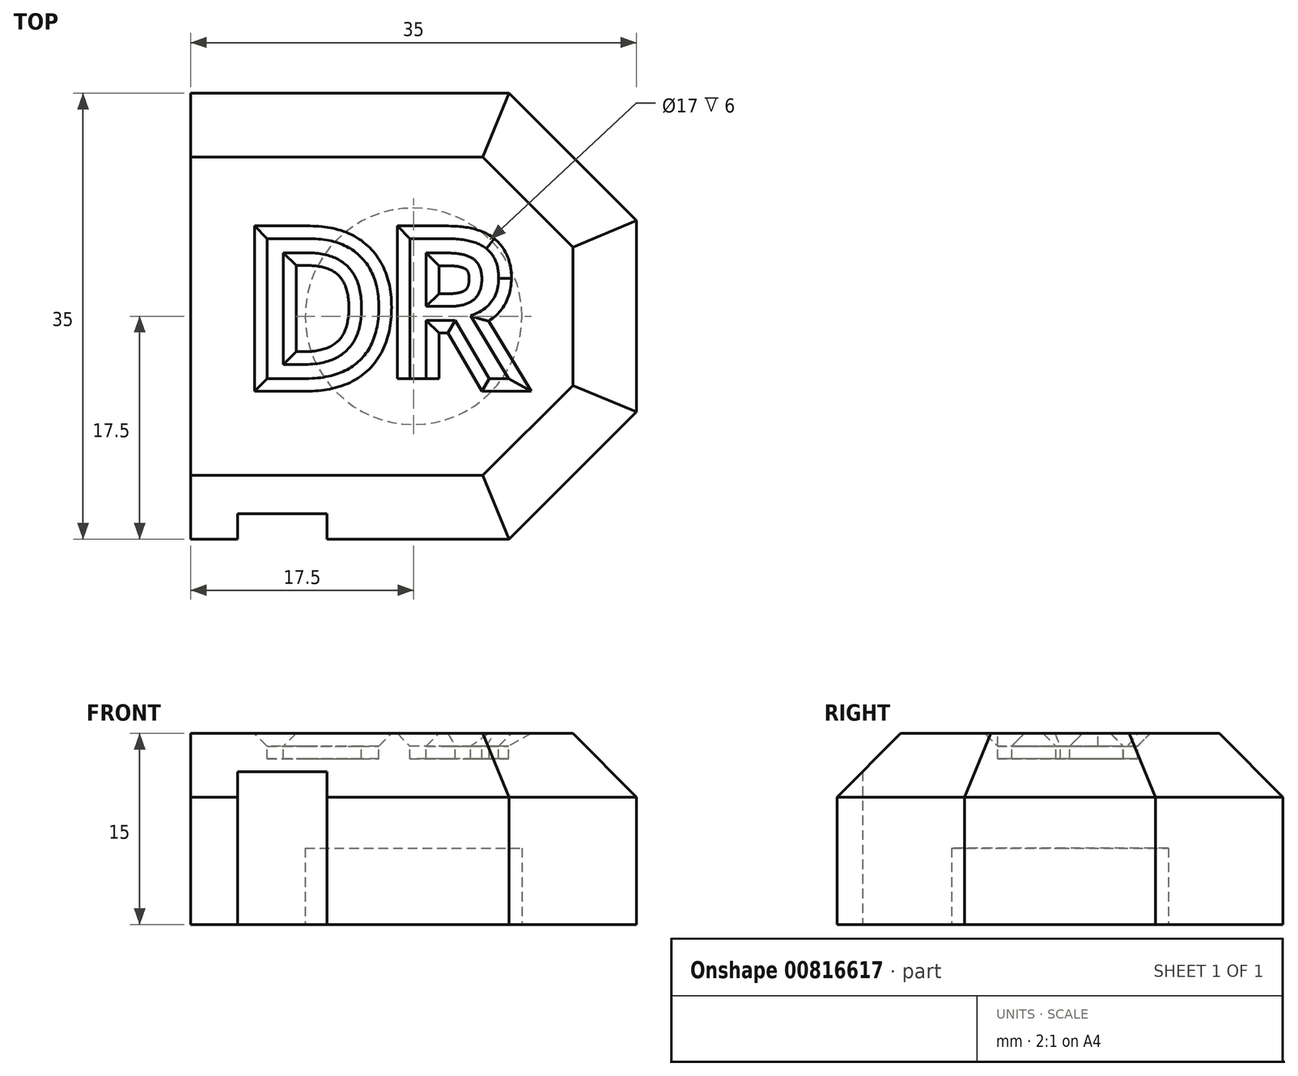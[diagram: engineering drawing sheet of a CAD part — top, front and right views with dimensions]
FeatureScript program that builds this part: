
annotation { "Feature Type Name" : "Feature", "Feature Type Description" : "" }
export const myFeature = defineFeature(function(context is Context, id is Id, definition is map)
    precondition{}
    {
        {
            var Q0;
            Q0=qCreatedBy(makeId("Top.planeOp"),FACE);
            var sketch = newSketch(context, id + "F0", { "sketchPlane" : qUnion([Q0])});
            skLineSegment(sketch, "E0.bottom", {"start": v(-17.5, 17.5) * mm, "end": v(17.5, 17.5) * mm});
            skLineSegment(sketch, "E0.top", {"start": v(-17.5, -17.5) * mm, "end": v(17.5, -17.5) * mm});
            skLineSegment(sketch, "E0.left", {"start": v(-17.5, 17.5) * mm, "end": v(-17.5, -17.5) * mm});
            skLineSegment(sketch, "E0.right", {"start": v(17.5, 17.5) * mm, "end": v(17.5, -17.5) * mm});
            skPoint(sketch, "E0.middle", {"position": v(0, 0) * mm});
            skSolve(sketch);
        }
        {
            var Q0;
            Q0=makeQuery(id+"F0.imprint","IMPRINT",FACE,{"disambiguationData":[TD([[makeQuery(id+"F0.imprint","IMPRINT",EDGE,{"derivedFrom":sQuery(id+"F0.wireOp",EDGE,"E0.bottom")}),-1.0]])]});
            extrude(context, id + "F1", {"entities" : qUnion([Q0]), "depth" : 15 * mm, "offsetDistance" : 25 * mm});
        }
        {
            var Q0;
            Q0=makeQuery(id+"F1.opExtrude","SWEPT_EDGE",EDGE,{"disambiguationData":[OSD([sQuery(id+"F0.wireOp",EDGE,"E0.top"),sQuery(id+"F0.wireOp",EDGE,"E0.right")])]});
            var Q1;
            Q1=makeQuery(id+"F1.opExtrude","SWEPT_EDGE",EDGE,{"disambiguationData":[OSD([sQuery(id+"F0.wireOp",EDGE,"E0.bottom"),sQuery(id+"F0.wireOp",EDGE,"E0.right")])]});
            chamfer(context, id + "F2", {"entities" : qUnion([Q0, Q1]), "width" : 10 * mm, "tangentPropagation" : true});
        }
        {
            var Q0;
            Q0=makeQuery(id+"F1.opExtrude","SWEPT_FACE",FACE,{"disambiguationData":[OSD([sQuery(id+"F0.wireOp",EDGE,"E0.top")])]});
            var sketch = newSketch(context, id + "F3", { "sketchPlane" : qUnion([Q0])});
            skLineSegment(sketch, "E1.bottom", {"start": v(-13.8, 12) * mm, "end": v(-6.8, 12) * mm});
            skLineSegment(sketch, "E1.top", {"start": v(-13.8, 0) * mm, "end": v(-6.8, 0) * mm});
            skLineSegment(sketch, "E1.left", {"start": v(-13.8, 12) * mm, "end": v(-13.8, 0) * mm});
            skLineSegment(sketch, "E1.right", {"start": v(-6.8, 12) * mm, "end": v(-6.8, 0) * mm});
            skSolve(sketch);
        }
        {
            var Q0;
            Q0=makeQuery(id+"F3.imprint","IMPRINT",FACE,{"disambiguationData":[TD([[makeQuery(id+"F3.imprint","IMPRINT",EDGE,{"derivedFrom":sQuery(id+"F3.wireOp",EDGE,"E1.bottom")}),-1.0]])]});
            extrude(context, id + "F4", {"entities" : qUnion([Q0]), "operationType" : NewBodyOperationType.REMOVE, "oppositeDirection" : true, "depth" : 2 * mm, "offsetDistance" : 25 * mm});
        }
        {
            var Q0;
            Q0=makeQuery(id+"F1.opExtrude","CAP_FACE",FACE,{"disambiguationData":[OSD([sQuery(id+"F0.wireOp",EDGE,"E0.bottom"),sQuery(id+"F0.wireOp",EDGE,"E0.top"),sQuery(id+"F0.wireOp",EDGE,"E0.left"),sQuery(id+"F0.wireOp",EDGE,"E0.right")])],"isStart":true});
            var sketch = newSketch(context, id + "F5", { "sketchPlane" : qUnion([Q0])});
            skCircle(sketch, "E2", {"center": v(0, 0) * mm, "radius": 8.5 * mm});
            skSolve(sketch);
        }
        {
            var Q0;
            Q0 = qSketchRegion(id + "F5", true);
            extrude(context, id + "F6", {"entities" : qUnion([Q0]), "operationType" : NewBodyOperationType.REMOVE, "oppositeDirection" : true, "depth" : 6 * mm, "offsetDistance" : 25 * mm});
        }
        {
            var Q0;
            {var subQ0=sQuery(id+"F0.wireOp",EDGE,"E0.right");var subQ1=sQuery(id+"F0.wireOp",EDGE,"E0.top");Q0=makeQuery(id+"F2.opChamfer","BLEND_EDGE",EDGE,{"blendedFrom":[makeQuery(id+"F1.opExtrude","SWEPT_EDGE",EDGE,{"disambiguationData":[OSD([subQ1,subQ0])]}),makeQuery(id+"F1.opExtrude","CAP_FACE",FACE,{"disambiguationData":[OSD([sQuery(id+"F0.wireOp",EDGE,"E0.bottom"),subQ1,sQuery(id+"F0.wireOp",EDGE,"E0.left"),subQ0])],"isStart":false})],"blendedInto":[makeQuery(id+"F1.opExtrude","CAP_FACE",FACE,{"disambiguationData":[OSD([sQuery(id+"F0.wireOp",EDGE,"E0.bottom"),subQ1,sQuery(id+"F0.wireOp",EDGE,"E0.left"),subQ0])],"isStart":false})]});}
            var Q1;
            Q1=makeQuery(id+"F1.opExtrude","CAP_EDGE",EDGE,{"disambiguationData":[OSD([sQuery(id+"F0.wireOp",EDGE,"E0.right")])],"isStart":false});
            var Q2;
            Q2=makeQuery(id+"F1.opExtrude","CAP_EDGE",EDGE,{"disambiguationData":[OSD([sQuery(id+"F0.wireOp",EDGE,"E0.bottom")])],"isStart":false});
            var Q3;
            {var subQ0=sQuery(id+"F0.wireOp",EDGE,"E0.right");var subQ1=sQuery(id+"F0.wireOp",EDGE,"E0.bottom");Q3=makeQuery(id+"F2.opChamfer","BLEND_EDGE",EDGE,{"blendedFrom":[makeQuery(id+"F1.opExtrude","SWEPT_EDGE",EDGE,{"disambiguationData":[OSD([subQ1,subQ0])]}),makeQuery(id+"F1.opExtrude","CAP_FACE",FACE,{"disambiguationData":[OSD([subQ1,sQuery(id+"F0.wireOp",EDGE,"E0.top"),sQuery(id+"F0.wireOp",EDGE,"E0.left"),subQ0])],"isStart":false})],"blendedInto":[makeQuery(id+"F1.opExtrude","CAP_FACE",FACE,{"disambiguationData":[OSD([subQ1,sQuery(id+"F0.wireOp",EDGE,"E0.top"),sQuery(id+"F0.wireOp",EDGE,"E0.left"),subQ0])],"isStart":false})]});}
            var Q4;
            Q4=makeQuery(id+"F1.opExtrude","CAP_EDGE",EDGE,{"disambiguationData":[OSD([sQuery(id+"F0.wireOp",EDGE,"E0.top")])],"isStart":false});
            chamfer(context, id + "F7", {"entities" : qUnion([Q0, Q1, Q2, Q3, Q4]), "width" : 5 * mm, "tangentPropagation" : true});
        }
        {
            var Q0;
            Q0=makeQuery(id+"F1.opExtrude","CAP_FACE",FACE,{"disambiguationData":[OSD([sQuery(id+"F0.wireOp",EDGE,"E0.bottom"),sQuery(id+"F0.wireOp",EDGE,"E0.top"),sQuery(id+"F0.wireOp",EDGE,"E0.left"),sQuery(id+"F0.wireOp",EDGE,"E0.right")])],"isStart":false});
            var sketch = newSketch(context, id + "F8", { "sketchPlane" : qUnion([Q0])});
            skText(sketch, "E3", { "text": "DR", "fontName": "OpenSans-Regular.ttf"});
            const initialGuessF8  = {"E3": [-0.013, -0.00489, 1, 0, 0.01107]};
            skSetInitialGuess(sketch, initialGuessF8);
            skSolve(sketch);
        }
        {
            var Q0;
            Q0 = qSketchRegion(id + "F8", true);
            extrude(context, id + "F9", {"entities" : qUnion([Q0]), "operationType" : NewBodyOperationType.REMOVE, "oppositeDirection" : true, "depth" : 2 * mm, "offsetDistance" : 25 * mm});
        }
        {
            var Q0;
            Q0=makeQuery(id+"F9.boolean.opBoolean","COPY",EDGE,{"derivedFrom":makeQuery(id+"F9.opExtrude","CAP_EDGE",EDGE,{"disambiguationData":[OSD([sQuery(id+"F8.wireOp",EDGE,"E3.sketch_text.stroke-4")])],"isStart":true})});
            var Q1;
            Q1=makeQuery(id+"F9.boolean.opBoolean","COPY",EDGE,{"derivedFrom":makeQuery(id+"F9.opExtrude","CAP_EDGE",EDGE,{"disambiguationData":[OSD([sQuery(id+"F8.wireOp",EDGE,"E3.sketch_text.stroke-3")])],"isStart":true})});
            var Q2;
            Q2=makeQuery(id+"F9.boolean.opBoolean","COPY",EDGE,{"derivedFrom":makeQuery(id+"F9.opExtrude","CAP_EDGE",EDGE,{"disambiguationData":[OSD([sQuery(id+"F8.wireOp",EDGE,"E3.sketch_text.stroke-18")])],"isStart":true})});
            var Q3;
            Q3=makeQuery(id+"F9.boolean.opBoolean","COPY",EDGE,{"derivedFrom":makeQuery(id+"F9.opExtrude","CAP_EDGE",EDGE,{"disambiguationData":[OSD([sQuery(id+"F8.wireOp",EDGE,"E3.sketch_text.stroke-21")])],"isStart":true})});
            var Q4;
            Q4=makeQuery(id+"F9.boolean.opBoolean","COPY",EDGE,{"derivedFrom":makeQuery(id+"F9.opExtrude","CAP_EDGE",EDGE,{"disambiguationData":[OSD([sQuery(id+"F8.wireOp",EDGE,"E3.sketch_text.stroke-22")])],"isStart":true})});
            var Q5;
            Q5=makeQuery(id+"F9.boolean.opBoolean","COPY",EDGE,{"derivedFrom":makeQuery(id+"F9.opExtrude","CAP_EDGE",EDGE,{"disambiguationData":[OSD([sQuery(id+"F8.wireOp",EDGE,"E3.sketch_text.stroke-23")])],"isStart":true})});
            var Q6;
            Q6=makeQuery(id+"F9.boolean.opBoolean","COPY",EDGE,{"derivedFrom":makeQuery(id+"F9.opExtrude","CAP_EDGE",EDGE,{"disambiguationData":[OSD([sQuery(id+"F8.wireOp",EDGE,"E3.sketch_text.stroke-24")])],"isStart":true})});
            var Q7;
            Q7=makeQuery(id+"F9.boolean.opBoolean","COPY",EDGE,{"derivedFrom":makeQuery(id+"F9.opExtrude","CAP_EDGE",EDGE,{"disambiguationData":[OSD([sQuery(id+"F8.wireOp",EDGE,"E3.sketch_text.stroke-14")])],"isStart":true})});
            var Q8;
            Q8=makeQuery(id+"F9.boolean.opBoolean","COPY",EDGE,{"derivedFrom":makeQuery(id+"F9.opExtrude","CAP_EDGE",EDGE,{"disambiguationData":[OSD([sQuery(id+"F8.wireOp",EDGE,"E3.sketch_text.stroke-16")])],"isStart":true})});
            chamfer(context, id + "F10", {"entities" : qUnion([Q0, Q1, Q2, Q3, Q4, Q5, Q6, Q7, Q8]), "width" : 1 * mm, "tangentPropagation" : true});
        }
        {
            var Q0;
            Q0=makeQuery(id+"F9.boolean.opBoolean","SPLIT",FACE,{"disambiguationData":[TD([makeQuery(id+"F9.opExtrude","SWEPT_FACE",FACE,{"disambiguationData":[OSD([sQuery(id+"F8.wireOp",EDGE,"E3.sketch_text.stroke-7")])]})])],"derivedFrom":makeQuery(id+"F1.opExtrude","CAP_FACE",FACE,{"disambiguationData":[OSD([sQuery(id+"F0.wireOp",EDGE,"E0.bottom"),sQuery(id+"F0.wireOp",EDGE,"E0.top"),sQuery(id+"F0.wireOp",EDGE,"E0.left"),sQuery(id+"F0.wireOp",EDGE,"E0.right")])],"isStart":false})});
            var Q1;
            Q1=makeQuery(id+"F9.boolean.opBoolean","SPLIT",FACE,{"disambiguationData":[TD([makeQuery(id+"F9.opExtrude","SWEPT_FACE",FACE,{"disambiguationData":[OSD([sQuery(id+"F8.wireOp",EDGE,"E3.sketch_text.stroke-25")])]})])],"derivedFrom":makeQuery(id+"F1.opExtrude","CAP_FACE",FACE,{"disambiguationData":[OSD([sQuery(id+"F0.wireOp",EDGE,"E0.bottom"),sQuery(id+"F0.wireOp",EDGE,"E0.top"),sQuery(id+"F0.wireOp",EDGE,"E0.left"),sQuery(id+"F0.wireOp",EDGE,"E0.right")])],"isStart":false})});
            chamfer(context, id + "F11", {"entities" : qUnion([Q0, Q1]), "width" : 1 * mm, "tangentPropagation" : true});
        }
    });
